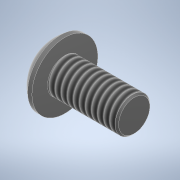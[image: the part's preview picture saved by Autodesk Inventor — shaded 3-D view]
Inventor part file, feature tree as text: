
AUTODESK INVENTOR PART (.ipt)
format: ipt  version: 2022 (Build 260153000, 153)  size: 146,944 bytes
history: native  units: mm
features: sketch x2, revolve x1, extrude x1, chamfer x1, thread x1
ambient origin geometry x8: Origin, YZ Plane, XZ Plane, XY Plane, X Axis, Y Axis, Z Axis, Center Point
bodies: Solid1 (feature_tree)
feature tree (6):
  revolve  "Revolution1"  [1 undecoded]
  extrude  "Extrusion1"  Depth=2.0mm
  chamfer  "Chamfer1"  Distance=2.0mm
  thread  "Thread1"  [1 undecoded]
  sketch  "Sketch1"  dims[d0=2.2mm d1=8.0mm]
  sketch  "Sketch2"  dims[d2=3.8mm d4=0.5mm d5=2.0mm d6=90.0deg d7=1.5mm d8=2.5mm d9=1.3mm d10=0.0mm d11=0.2mm d12=2.0mm d13=45.0deg d14=7.8mm d15=0.0mm]
note: 2 required parameter values undecoded (feature->parameter linkage not recoverable at this tier; creation-order binding heuristic only, values carry confidence <= 0.55)